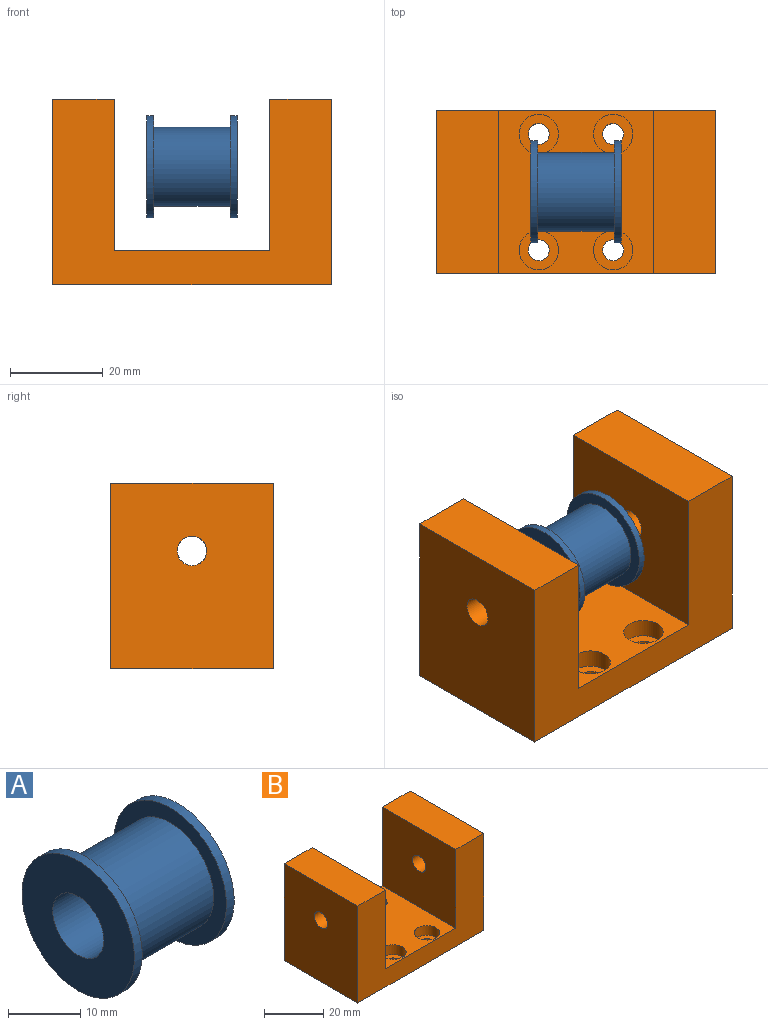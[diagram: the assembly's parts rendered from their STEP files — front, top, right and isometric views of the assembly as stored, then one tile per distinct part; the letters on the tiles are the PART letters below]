
ASSEMBLY  parts=2 mates=1
PART A: 8 faces, bbox 19.5x22x22 mm
  f0: cylinder r=11mm len=22mm, axis (-1,0,0), area 103.7mm2, adj f4,f6
  f1: cylinder r=5mm len=19.5mm, axis (-1,0,0), area 612.6mm2, adj f3,f4
  f2: cylinder r=11mm len=22mm, axis (-1,0,0), area 103.7mm2, adj f3,f7
  f3: plane 22x22mm, normal (1,0,0), area 301.6mm2, adj f1,f2
  f4: plane 22x22mm, normal (-1,0,0), area 301.6mm2, adj f0,f1
  f5: cylinder r=8.5mm len=17mm, axis (1,0,0), area 881.2mm2, adj f6,f7
  f6: plane 22x22mm, normal (1,0,0), area 153.2mm2, adj f0,f5
  f7: plane 22x22mm, normal (-1,0,0), area 153.2mm2, adj f2,f5
PART B: 24 faces, bbox 60x35x40 mm
  f0: plane 40x35mm, normal (1,0,0), area 1368.3mm2, adj f1,f7,f8,f9,f23
  f1: plane 35x13.25mm, normal (0,0,1), area 463.7mm2, adj f0,f2,f8,f9
  f2: plane 35x32.5mm, normal (-1,0,0), area 1105.8mm2, adj f1,f3,f8,f9,f23
  f3: plane 35x33.5mm, normal (0,0,1), area 945.5mm2, adj f2,f4,f8,f9,f10,f12,f14,f16
  f4: plane 35x32.5mm, normal (1,0,0), area 1105.8mm2, adj f3,f5,f8,f9,f22
  f5: plane 35x13.25mm, normal (0,0,1), area 463.7mm2, adj f4,f6,f8,f9
  f6: plane 40x35mm, normal (-1,0,0), area 1368.3mm2, adj f5,f7,f8,f9,f22
  f7: plane 60x35mm, normal (0,0,-1), area 2036.4mm2, adj f0,f6,f8,f9,f18,f19,f20,f21
  f8: plane 60x40mm, normal (0,-1,0), area 1311.2mm2, adj f0,f1,f2,f3,f4,f5,f6,f7
  f9: plane 60x40mm, normal (0,1,0), area 1311.2mm2, adj f0,f1,f2,f3,f4,f5,f6,f7
  f10: cylinder r=4.25mm len=8.5mm, axis (0,0,1), area 106.8mm2, adj f3,f11
  f11: plane 8.5x8.5mm, normal (0,0,1), area 40.8mm2, adj f10,f21
  f12: cylinder r=4.25mm len=8.5mm, axis (0,0,1), area 106.8mm2, adj f3,f13
  f13: plane 8.5x8.5mm, normal (0,0,1), area 40.8mm2, adj f12,f18
  f14: cylinder r=4.25mm len=8.5mm, axis (0,0,1), area 106.8mm2, adj f3,f15
  f15: plane 8.5x8.5mm, normal (0,0,1), area 40.8mm2, adj f14,f19
  f16: cylinder r=4.25mm len=8.5mm, axis (0,0,1), area 106.8mm2, adj f3,f17
  f17: plane 8.5x8.5mm, normal (0,0,1), area 40.8mm2, adj f16,f20
  f18: cylinder r=2.25mm len=4.5mm, axis (0,0,1), area 49.5mm2, adj f7,f13
  f19: cylinder r=2.25mm len=4.5mm, axis (0,0,1), area 49.5mm2, adj f7,f15
  f20: cylinder r=2.25mm len=4.5mm, axis (0,0,1), area 49.5mm2, adj f7,f17
  f21: cylinder r=2.25mm len=4.5mm, axis (0,0,1), area 49.5mm2, adj f7,f11
  f22: cylinder r=3.17mm len=13.25mm, axis (1,0,0), area 264.3mm2, adj f4,f6
  f23: cylinder r=3.17mm len=13.25mm, axis (1,0,0), area 264.3mm2, adj f0,f2
PLACE A t=(-0.01,0,0)mm
PLACE B at identity fixed
MATE fastened A.f0 <-> B.f22  axis (1,0,0) through (9.74,0,25.4)mm
